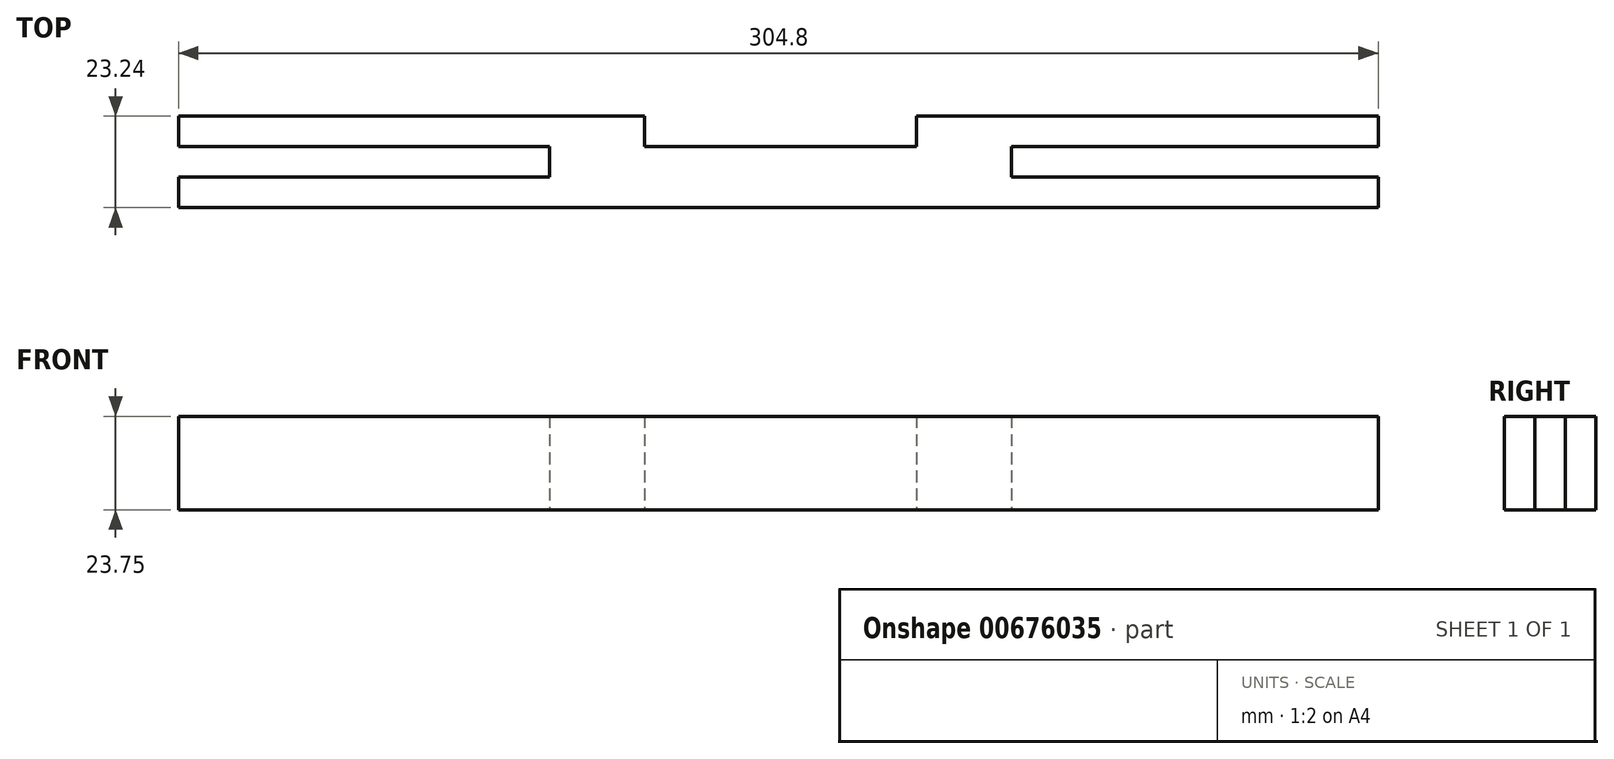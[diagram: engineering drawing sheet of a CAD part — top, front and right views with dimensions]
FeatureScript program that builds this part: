
annotation { "Feature Type Name" : "Feature", "Feature Type Description" : "" }
export const myFeature = defineFeature(function(context is Context, id is Id, definition is map)
    precondition{}
    {
        {
            var Q0;
            Q0=qCreatedBy(makeId("Top.planeOp"),FACE);
            var sketch = newSketch(context, id + "F0", { "sketchPlane" : qUnion([Q0])});
            skLineSegment(sketch, "E0", {"start": v(-160.44, 0) * mm, "end": v(144.36, 0) * mm});
            skLineSegment(sketch, "E1", {"start": v(144.36, 0) * mm, "end": v(144.36, 7.75) * mm});
            skLineSegment(sketch, "E2", {"start": v(144.36, 7.75) * mm, "end": v(51.14, 7.75) * mm});
            skLineSegment(sketch, "E3", {"start": v(51.14, 7.75) * mm, "end": v(51.14, 15.5) * mm});
            skLineSegment(sketch, "E4", {"start": v(51.14, 15.5) * mm, "end": v(144.36, 15.5) * mm});
            skLineSegment(sketch, "E5", {"start": v(144.36, 15.5) * mm, "end": v(144.36, 23.24) * mm});
            skLineSegment(sketch, "E6", {"start": v(144.36, 23.24) * mm, "end": v(27.01, 23.24) * mm});
            skLineSegment(sketch, "E7", {"start": v(27.01, 23.24) * mm, "end": v(27.01, 15.5) * mm});
            skLineSegment(sketch, "E8", {"start": v(27.01, 15.5) * mm, "end": v(-42.08, 15.5) * mm});
            skLineSegment(sketch, "E9", {"start": v(-42.08, 15.5) * mm, "end": v(-42.08, 23.24) * mm});
            skLineSegment(sketch, "E10", {"start": v(-42.08, 23.24) * mm, "end": v(-160.44, 23.24) * mm});
            skLineSegment(sketch, "E11", {"start": v(-160.44, 23.24) * mm, "end": v(-160.44, 15.5) * mm});
            skLineSegment(sketch, "E12", {"start": v(-160.44, 15.5) * mm, "end": v(-66.2, 15.5) * mm});
            skLineSegment(sketch, "E13", {"start": v(-66.2, 15.5) * mm, "end": v(-66.2, 7.75) * mm});
            skLineSegment(sketch, "E14", {"start": v(-160.44, 0) * mm, "end": v(-160.44, 7.75) * mm});
            skLineSegment(sketch, "E15", {"start": v(-160.44, 7.75) * mm, "end": v(-66.2, 7.75) * mm});
            skSolve(sketch);
        }
        {
            var Q0;
            Q0=makeQuery(id+"F0.imprint","IMPRINT",FACE,{"disambiguationData":[TD([[makeQuery(id+"F0.imprint","IMPRINT",EDGE,{"derivedFrom":sQuery(id+"F0.wireOp",EDGE,"E0")}),1.0]])]});
            extrude(context, id + "F1", {"entities" : qUnion([Q0]), "depth" : 23.75 * mm, "offsetDistance" : 25.4 * mm});
        }
    });
